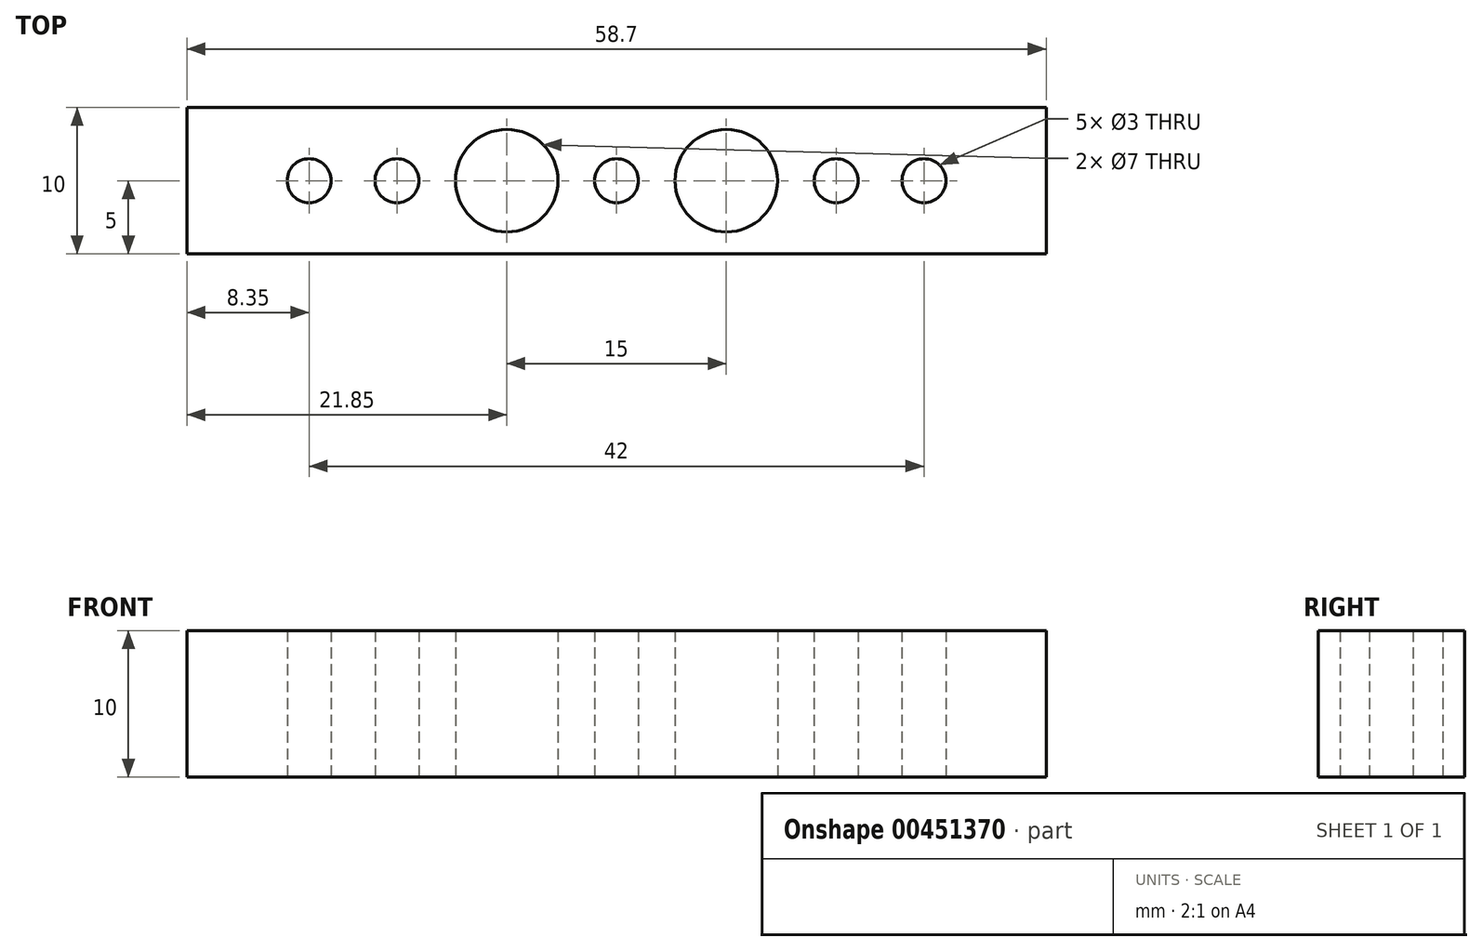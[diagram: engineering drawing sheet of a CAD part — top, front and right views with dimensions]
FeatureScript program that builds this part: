
annotation { "Feature Type Name" : "Feature", "Feature Type Description" : "" }
export const myFeature = defineFeature(function(context is Context, id is Id, definition is map)
    precondition{}
    {
        {
            var Q0;
            Q0=qCreatedBy(makeId("Top.planeOp"),FACE);
            var sketch = newSketch(context, id + "F0", { "sketchPlane" : qUnion([Q0])});
            skLineSegment(sketch, "E0.bottom", {"start": v(29.35, 5) * mm, "end": v(-29.35, 5) * mm});
            skLineSegment(sketch, "E0.top", {"start": v(29.35, -5) * mm, "end": v(-29.35, -5) * mm});
            skLineSegment(sketch, "E0.left", {"start": v(29.35, 5) * mm, "end": v(29.35, -5) * mm});
            skLineSegment(sketch, "E0.right", {"start": v(-29.35, 5) * mm, "end": v(-29.35, -5) * mm});
            skPoint(sketch, "E0.middle", {"position": v(0, 0) * mm});
            skCircle(sketch, "E1", {"center": v(-7.5, 0) * mm, "radius": 3.5 * mm});
            skPoint(sketch, "E1.centerSnap0", {"position": v(-29.35, 0) * mm});
            skCircle(sketch, "E2.MirrorC", {"center": v(7.5, 0) * mm, "radius": 3.5 * mm});
            skCircle(sketch, "E3", {"center": v(-21, 0) * mm, "radius": 1.5 * mm});
            skCircle(sketch, "E4.MirrorC", {"center": v(21, 0) * mm, "radius": 1.5 * mm});
            skCircle(sketch, "E5", {"center": v(-15, 0) * mm, "radius": 1.5 * mm});
            skCircle(sketch, "E6", {"center": v(0, 0) * mm, "radius": 1.5 * mm});
            skCircle(sketch, "E7.MirrorC", {"center": v(15, 0) * mm, "radius": 1.5 * mm});
            skCircle(sketch, "E8", {"center": v(0, 0) * mm, "radius": 3 * mm, "construction": true});
            skCircle(sketch, "E9", {"center": v(15, 0) * mm, "radius": 3 * mm, "construction": true});
            skCircle(sketch, "E10", {"center": v(-15, 0) * mm, "radius": 3 * mm, "construction": true});
            skSolve(sketch);
        }
        {
            var Q0;
            Q0=makeQuery(id+"F0.imprint","IMPRINT",FACE,{"disambiguationData":[TD([[makeQuery(id+"F0.imprint","IMPRINT",EDGE,{"derivedFrom":sQuery(id+"F0.wireOp",EDGE,"E0.bottom")}),1.0]])]});
            extrude(context, id + "F1", {"entities" : qUnion([Q0]), "depth" : 10 * mm});
        }
    });
